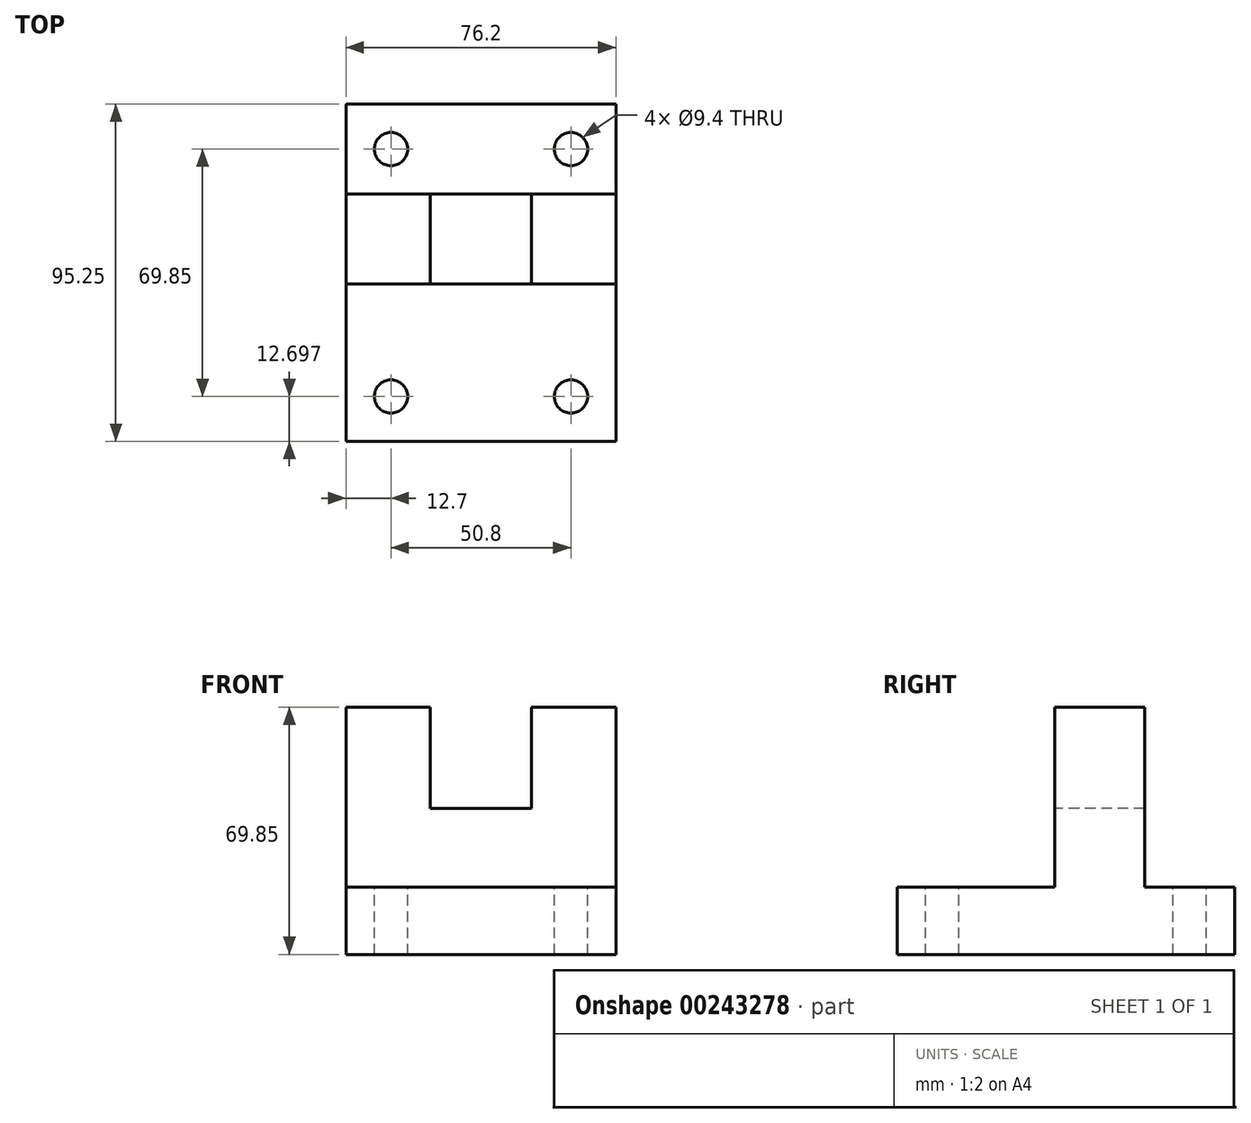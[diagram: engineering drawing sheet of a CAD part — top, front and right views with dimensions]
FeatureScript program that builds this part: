
annotation { "Feature Type Name" : "Feature", "Feature Type Description" : "" }
export const myFeature = defineFeature(function(context is Context, id is Id, definition is map)
    precondition{}
    {
        {
            var Q0;
            Q0=qCreatedBy(makeId("Right.planeOp"),FACE);
            var sketch = newSketch(context, id + "F0", { "sketchPlane" : qUnion([Q0])});
            skLineSegment(sketch, "E0", {"start": v(-31.17, 0) * mm, "end": v(-31.17, 19.05) * mm});
            skLineSegment(sketch, "E1", {"start": v(-31.17, 19.05) * mm, "end": v(13.28, 19.05) * mm});
            skLineSegment(sketch, "E2", {"start": v(13.28, 19.05) * mm, "end": v(13.28, 69.85) * mm});
            skLineSegment(sketch, "E3", {"start": v(13.28, 69.85) * mm, "end": v(38.68, 69.85) * mm});
            skLineSegment(sketch, "E4", {"start": v(38.68, 69.85) * mm, "end": v(38.68, 19.05) * mm});
            skLineSegment(sketch, "E5", {"start": v(38.68, 19.05) * mm, "end": v(64.08, 19.05) * mm});
            skLineSegment(sketch, "E6", {"start": v(64.08, 19.05) * mm, "end": v(64.08, 0) * mm});
            skLineSegment(sketch, "E7", {"start": v(64.08, 0) * mm, "end": v(-31.17, 0) * mm});
            skSolve(sketch);
        }
        {
            var Q0;
            Q0=makeQuery(id+"F0.imprint","IMPRINT",FACE,{"disambiguationData":[TD([[makeQuery(id+"F0.imprint","IMPRINT",EDGE,{"derivedFrom":sQuery(id+"F0.wireOp",EDGE,"E0")}),-1.0]])]});
            extrude(context, id + "F1", {"entities" : qUnion([Q0]), "oppositeDirection" : true, "depth" : 76.2 * mm});
        }
        {
            var Q0;
            Q0=makeQuery(id+"F1.opExtrude","SWEPT_FACE",FACE,{"disambiguationData":[OSD([sQuery(id+"F0.wireOp",EDGE,"E2")])]});
            var sketch = newSketch(context, id + "F2", { "sketchPlane" : qUnion([Q0])});
            skLineSegment(sketch, "E8", {"start": v(-52.37, 69.85) * mm, "end": v(-52.37, 46.17) * mm});
            skLineSegment(sketch, "E9", {"start": v(-52.37, 69.85) * mm, "end": v(-23.8, 69.85) * mm});
            skLineSegment(sketch, "E10", {"start": v(-23.8, 69.85) * mm, "end": v(-23.8, 41.27) * mm});
            skLineSegment(sketch, "E11", {"start": v(-23.8, 41.27) * mm, "end": v(-52.37, 41.27) * mm});
            skLineSegment(sketch, "E12", {"start": v(-52.37, 41.27) * mm, "end": v(-52.37, 69.85) * mm});
            skSolve(sketch);
        }
        {
            var Q0;
            {var subQ3=sQuery(id+"F2.wireOp",EDGE,"E9");Q0=makeQuery(id+"F2.imprint","IMPRINT",FACE,{"disambiguationData":[TD([[makeQuery(id+"F2.imprint","IMPRINT",EDGE,{"derivedFrom":subQ3}),-1.0]])]});}
            extrude(context, id + "F3", {"entities" : qUnion([Q0]), "operationType" : NewBodyOperationType.REMOVE, "endBound" : BoundingType.THROUGH_ALL, "oppositeDirection" : true, "depth" : 25.4 * mm});
        }
        {
            var Q0;
            Q0=makeQuery(id+"F1.opExtrude","SWEPT_FACE",FACE,{"disambiguationData":[OSD([sQuery(id+"F0.wireOp",EDGE,"E1")])]});
            var sketch = newSketch(context, id + "F4", { "sketchPlane" : qUnion([Q0])});
            skCircle(sketch, "E13", {"center": v(-12.7, -18.47) * mm, "radius": 4.7 * mm});
            skCircle(sketch, "E14", {"center": v(-63.5, -18.47) * mm, "radius": 4.7 * mm});
            skSolve(sketch);
        }
        {
            var Q0;
            Q0=makeQuery(id+"F1.opExtrude","SWEPT_FACE",FACE,{"disambiguationData":[OSD([sQuery(id+"F0.wireOp",EDGE,"E5")])]});
            var sketch = newSketch(context, id + "F5", { "sketchPlane" : qUnion([Q0])});
            skCircle(sketch, "E15", {"center": v(-63.5, 51.38) * mm, "radius": 4.7 * mm});
            skCircle(sketch, "E16", {"center": v(-12.7, 51.38) * mm, "radius": 4.7 * mm});
            skSolve(sketch);
        }
        {
            var Q0;
            Q0=makeQuery(id+"F5.imprint","IMPRINT",FACE,{"disambiguationData":[TD([[makeQuery(id+"F5.imprint","IMPRINT",EDGE,{"derivedFrom":sQuery(id+"F5.wireOp",EDGE,"E15")}),1.0]])]});
            var Q1;
            Q1=makeQuery(id+"F5.imprint","IMPRINT",FACE,{"disambiguationData":[TD([[makeQuery(id+"F5.imprint","IMPRINT",EDGE,{"derivedFrom":sQuery(id+"F5.wireOp",EDGE,"E16")}),1.0]])]});
            extrude(context, id + "F6", {"entities" : qUnion([Q0, Q1]), "operationType" : NewBodyOperationType.REMOVE, "endBound" : BoundingType.THROUGH_ALL, "oppositeDirection" : true, "depth" : 25.4 * mm});
        }
        {
            var Q0;
            Q0=makeQuery(id+"F4.imprint","IMPRINT",FACE,{"disambiguationData":[TD([[makeQuery(id+"F4.imprint","IMPRINT",EDGE,{"derivedFrom":sQuery(id+"F4.wireOp",EDGE,"E14")}),1.0]])]});
            var Q1;
            Q1=makeQuery(id+"F4.imprint","IMPRINT",FACE,{"disambiguationData":[TD([[makeQuery(id+"F4.imprint","IMPRINT",EDGE,{"derivedFrom":sQuery(id+"F4.wireOp",EDGE,"E13")}),1.0]])]});
            extrude(context, id + "F7", {"entities" : qUnion([Q0, Q1]), "operationType" : NewBodyOperationType.REMOVE, "endBound" : BoundingType.THROUGH_ALL, "oppositeDirection" : true, "depth" : 25.4 * mm});
        }
    });
